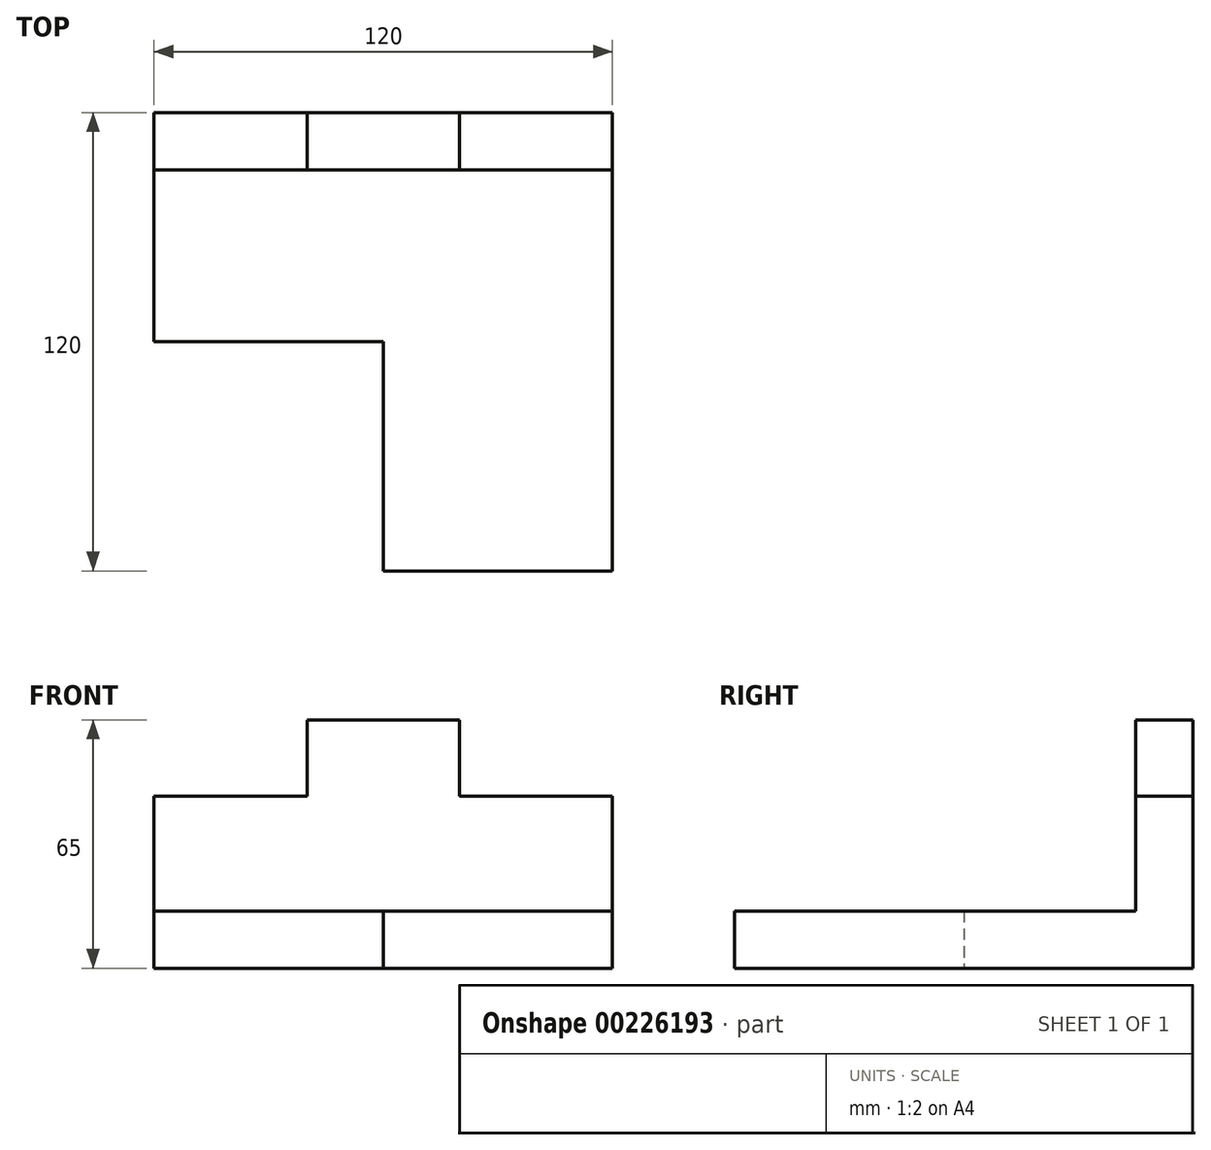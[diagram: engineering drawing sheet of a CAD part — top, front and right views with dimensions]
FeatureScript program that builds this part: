
annotation { "Feature Type Name" : "Feature", "Feature Type Description" : "" }
export const myFeature = defineFeature(function(context is Context, id is Id, definition is map)
    precondition{}
    {
        {
            var Q0;
            Q0=qCreatedBy(makeId("Top.planeOp"),FACE);
            var sketch = newSketch(context, id + "F0", { "sketchPlane" : qUnion([Q0])});
            skLineSegment(sketch, "E0.bottom", {"start": v(0, 0) * mm, "end": v(-120, 0) * mm});
            skLineSegment(sketch, "E0.top", {"start": v(0, -120) * mm, "end": v(-120, -120) * mm});
            skLineSegment(sketch, "E0.left", {"start": v(0, 0) * mm, "end": v(0, -120) * mm});
            skLineSegment(sketch, "E0.right", {"start": v(-120, 0) * mm, "end": v(-120, -120) * mm});
            skPoint(sketch, "E1.oppositeSnap0", {"position": v(0, -60) * mm});
            skLineSegment(sketch, "E1.bottom", {"start": v(-120, -120) * mm, "end": v(-60, -120) * mm});
            skLineSegment(sketch, "E1.top", {"start": v(-120, -60) * mm, "end": v(-60, -60) * mm});
            skLineSegment(sketch, "E1.left", {"start": v(-120, -120) * mm, "end": v(-120, -60) * mm});
            skLineSegment(sketch, "E1.right", {"start": v(-60, -120) * mm, "end": v(-60, -60) * mm});
            skSolve(sketch);
        }
        {
            var Q0;
            Q0=makeQuery(id+"F0.imprint","IMPRINT",FACE,{"disambiguationData":[TD([[makeQuery(id+"F0.imprint","IMPRINT",EDGE,{"derivedFrom":sQuery(id+"F0.wireOp",EDGE,"E0.bottom")}),1.0]])]});
            extrude(context, id + "F1", {"entities" : qUnion([Q0]), "depth" : 15 * mm});
        }
        {
            var Q0;
            Q0=makeQuery(id+"F1.opExtrude","SWEPT_FACE",FACE,{"disambiguationData":[OSD([sQuery(id+"F0.wireOp",EDGE,"E0.bottom")])]});
            var sketch = newSketch(context, id + "F2", { "sketchPlane" : qUnion([Q0])});
            skPoint(sketch, "E2.oppositeSnap0", {"position": v(120, 7.5) * mm});
            skLineSegment(sketch, "E2.bottom", {"start": v(0, 0) * mm, "end": v(120, 0) * mm});
            skLineSegment(sketch, "E2.top", {"start": v(0, 65) * mm, "end": v(120, 65) * mm});
            skLineSegment(sketch, "E2.left", {"start": v(0, 0) * mm, "end": v(0, 65) * mm});
            skLineSegment(sketch, "E2.right", {"start": v(120, 0) * mm, "end": v(120, 65) * mm});
            skLineSegment(sketch, "E3.bottom", {"start": v(0, 65) * mm, "end": v(40, 65) * mm});
            skLineSegment(sketch, "E3.top", {"start": v(0, 45) * mm, "end": v(40, 45) * mm});
            skLineSegment(sketch, "E3.left", {"start": v(0, 65) * mm, "end": v(0, 45) * mm});
            skLineSegment(sketch, "E3.right", {"start": v(40, 65) * mm, "end": v(40, 45) * mm});
            skLineSegment(sketch, "E4", {"start": v(60, 65) * mm, "end": v(60, 0) * mm, "construction": true});
            skLineSegment(sketch, "E5.MirrorCS", {"start": v(80, 65) * mm, "end": v(80, 45) * mm});
            skLineSegment(sketch, "E6.MirrorCS", {"start": v(120, 45) * mm, "end": v(80, 45) * mm});
            skSolve(sketch);
        }
        {
            var Q0;
            {var subQ4=sQuery(id+"F2.wireOp",EDGE,"E3.top");Q0=makeQuery(id+"F2.imprint","IMPRINT",FACE,{"disambiguationData":[TD([[makeQuery(id+"F2.imprint","IMPRINT",EDGE,{"derivedFrom":subQ4}),-1.0]])]});}
            extrude(context, id + "F3", {"entities" : qUnion([Q0]), "operationType" : NewBodyOperationType.ADD, "oppositeDirection" : true, "depth" : 15 * mm});
        }
    });
